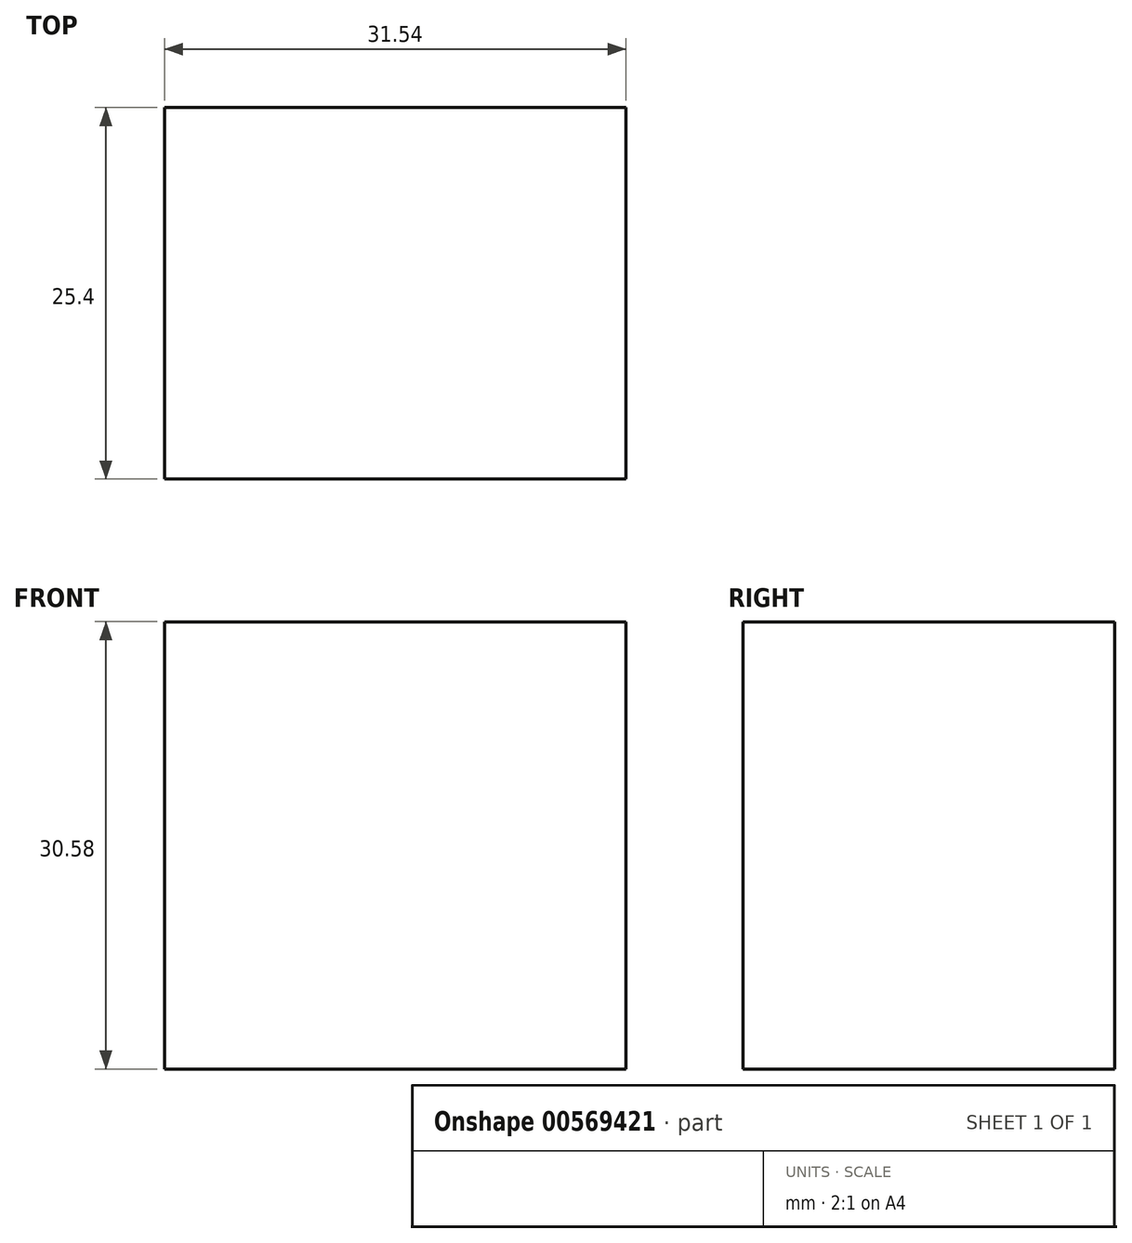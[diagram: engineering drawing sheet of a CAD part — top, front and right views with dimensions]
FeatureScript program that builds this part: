
annotation { "Feature Type Name" : "Feature", "Feature Type Description" : "" }
export const myFeature = defineFeature(function(context is Context, id is Id, definition is map)
    precondition{}
    {
        {
            var Q0;
            Q0=qCreatedBy(makeId("Front.planeOp"),FACE);
            var sketch = newSketch(context, id + "F0", { "sketchPlane" : qUnion([Q0])});
            skLineSegment(sketch, "E0.bottom", {"start": v(-36.63, 17.24) * mm, "end": v(-5.09, 17.24) * mm});
            skLineSegment(sketch, "E0.top", {"start": v(-36.63, -13.34) * mm, "end": v(-5.09, -13.34) * mm});
            skLineSegment(sketch, "E0.left", {"start": v(-36.63, 17.24) * mm, "end": v(-36.63, -13.34) * mm});
            skLineSegment(sketch, "E0.right", {"start": v(-5.09, 17.24) * mm, "end": v(-5.09, -13.34) * mm});
            skSolve(sketch);
        }
        {
            var Q0;
            Q0=makeQuery(id+"F0.imprint","IMPRINT",FACE,{"disambiguationData":[TD([[makeQuery(id+"F0.imprint","IMPRINT",EDGE,{"derivedFrom":sQuery(id+"F0.wireOp",EDGE,"E0.bottom")}),-1.0]])]});
            extrude(context, id + "F1", {"entities" : qUnion([Q0]), "depth" : 25.4 * mm, "offsetDistance" : 25.4 * mm});
        }
    });
